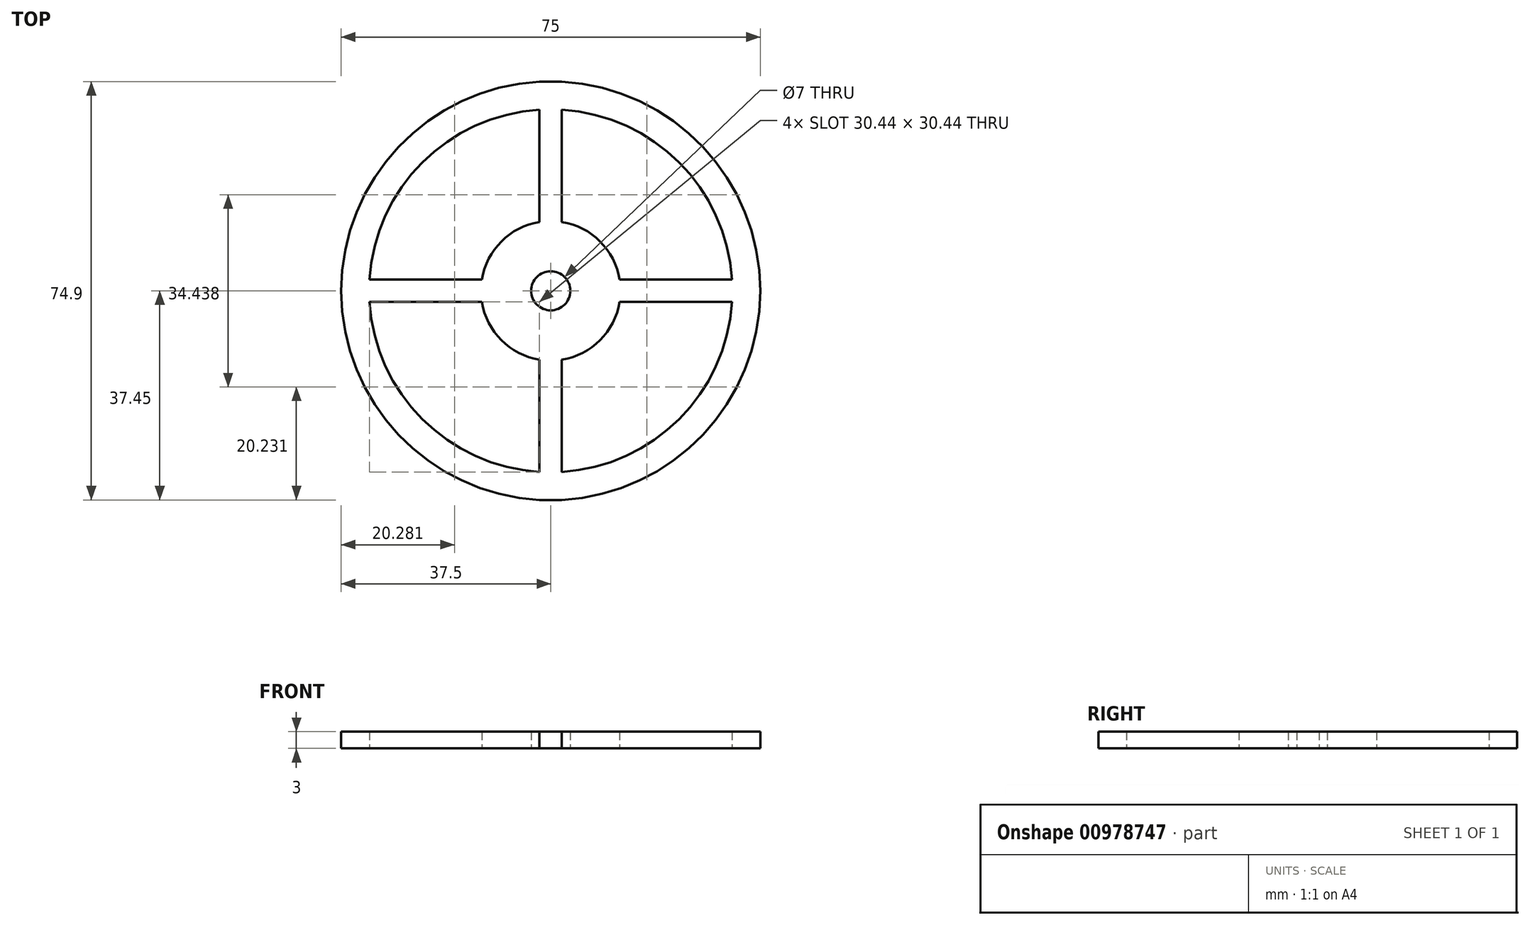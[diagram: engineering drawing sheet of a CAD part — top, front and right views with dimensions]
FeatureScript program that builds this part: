
annotation { "Feature Type Name" : "Feature", "Feature Type Description" : "" }
export const myFeature = defineFeature(function(context is Context, id is Id, definition is map)
    precondition{}
    {
        {
            var Q0;
            Q0=qCreatedBy(makeId("Top.planeOp"),FACE);
            var sketch = newSketch(context, id + "F0", { "sketchPlane" : qUnion([Q0])});
            skCircle(sketch, "E0", {"center": v(0, 0) * mm, "radius": 37.5 * mm});
            skCircle(sketch, "E1", {"center": v(0, 0) * mm, "radius": 3.5 * mm});
            skLineSegment(sketch, "E2", {"start": v(0, 0) * mm, "end": v(0, 37.5) * mm, "construction": true});
            skLineSegment(sketch, "E3", {"start": v(0, 0) * mm, "end": v(0, -37.5) * mm, "construction": true});
            skLineSegment(sketch, "E4", {"start": v(0, 0) * mm, "end": v(-37.5, 0) * mm, "construction": true});
            skLineSegment(sketch, "E5", {"start": v(0, 0) * mm, "end": v(37.5, 0) * mm, "construction": true});
            skLineSegment(sketch, "E6.bottom", {"start": v(-2, 2) * mm, "end": v(2, 2) * mm, "construction": true});
            skLineSegment(sketch, "E6.top", {"start": v(-2, -2) * mm, "end": v(2, -2) * mm, "construction": true});
            skLineSegment(sketch, "E6.left", {"start": v(-2, 2) * mm, "end": v(-2, -2) * mm, "construction": true});
            skLineSegment(sketch, "E6.right", {"start": v(2, 2) * mm, "end": v(2, -2) * mm, "construction": true});
            skLineSegment(sketch, "E7", {"start": v(-2, 2) * mm, "end": v(2, -2) * mm, "construction": true});
            skLineSegment(sketch, "E8.left", {"start": v(-2, 2) * mm, "end": v(-2, 0.65) * mm, "construction": true});
            skLineSegment(sketch, "E8.right", {"start": v(-37.45, -0.65) * mm, "end": v(-37.45, -2) * mm, "construction": true});
            skLineSegment(sketch, "E9.bottom", {"start": v(2, -2) * mm, "end": v(37.5, -2) * mm});
            skLineSegment(sketch, "E9.top", {"start": v(2, 2) * mm, "end": v(37.5, 2) * mm});
            skLineSegment(sketch, "E9.left", {"start": v(2, -2) * mm, "end": v(2, 2) * mm, "construction": true});
            skLineSegment(sketch, "E9.right", {"start": v(37.5, -2) * mm, "end": v(37.5, 2) * mm, "construction": true});
            skLineSegment(sketch, "E10.bottom", {"start": v(-2, 2) * mm, "end": v(-37.45, 2) * mm});
            skLineSegment(sketch, "E10.top", {"start": v(-2, -2) * mm, "end": v(-37.45, -2) * mm});
            skLineSegment(sketch, "E10.right", {"start": v(-37.45, 2) * mm, "end": v(-37.45, -2) * mm, "construction": true});
            skLineSegment(sketch, "E11.bottom", {"start": v(-2, 2) * mm, "end": v(2, 2) * mm});
            skLineSegment(sketch, "E11.top", {"start": v(-2, 37.45) * mm, "end": v(2, 37.45) * mm});
            skLineSegment(sketch, "E11.left", {"start": v(-2, 2) * mm, "end": v(-2, 37.45) * mm});
            skLineSegment(sketch, "E11.right", {"start": v(2, 2) * mm, "end": v(2, 37.45) * mm});
            skLineSegment(sketch, "E12.bottom", {"start": v(-2, -2) * mm, "end": v(2, -2) * mm});
            skLineSegment(sketch, "E12.top", {"start": v(-2, -37.45) * mm, "end": v(2, -37.45) * mm});
            skLineSegment(sketch, "E12.left", {"start": v(-2, -2) * mm, "end": v(-2, -37.45) * mm});
            skLineSegment(sketch, "E12.right", {"start": v(2, -2) * mm, "end": v(2, -37.45) * mm});
            skCircle(sketch, "E13", {"center": v(0, 0) * mm, "radius": 12.5 * mm});
            skCircle(sketch, "E14", {"center": v(0, 0) * mm, "radius": 32.5 * mm});
            skSolve(sketch);
        }
        {
            var Q0;
            {var subQ1=sQuery(id+"F0.wireOp",EDGE,"E0");var subQ3=sQuery(id+"F0.wireOp",EDGE,"E9.top");var subQ4=makeQuery(id+"F0.imprint","INTERSECT",VERTEX,{"derivedFrom":[subQ1,subQ3]});Q0=makeQuery(id+"F0.imprint","IMPRINT",FACE,{"disambiguationData":[TD([[makeQuery(id+"F0.imprint","IMPRINT",EDGE,{"disambiguationData":[TD([[subQ4,1.0]])],"derivedFrom":subQ3}),1.0]])]});}
            var Q1;
            {var subQ1=sQuery(id+"F0.wireOp",EDGE,"E0");var subQ3=sQuery(id+"F0.wireOp",EDGE,"E9.bottom");var subQ4=makeQuery(id+"F0.imprint","INTERSECT",VERTEX,{"derivedFrom":[subQ1,subQ3]});Q1=makeQuery(id+"F0.imprint","IMPRINT",FACE,{"disambiguationData":[TD([[makeQuery(id+"F0.imprint","IMPRINT",EDGE,{"disambiguationData":[TD([[subQ4,1.0]])],"derivedFrom":subQ3}),-1.0]])]});}
            var Q2;
            {var subQ0=sQuery(id+"F0.wireOp",EDGE,"E9.top");var subQ1=sQuery(id+"F0.wireOp",EDGE,"E0");var subQ2=makeQuery(id+"F0.imprint","INTERSECT",VERTEX,{"derivedFrom":[subQ1,subQ0]});Q2=makeQuery(id+"F0.imprint","IMPRINT",FACE,{"disambiguationData":[TD([[makeQuery(id+"F0.imprint","IMPRINT",EDGE,{"disambiguationData":[TD([[subQ2,1.0]])],"derivedFrom":subQ1}),1.0]])]});}
            var Q3;
            {var subQ0=sQuery(id+"F0.wireOp",EDGE,"E13");var subQ1=sQuery(id+"F0.wireOp",EDGE,"E9.bottom");var subQ2=makeQuery(id+"F0.imprint","INTERSECT",VERTEX,{"derivedFrom":[subQ1,subQ0]});Q3=makeQuery(id+"F0.imprint","IMPRINT",FACE,{"disambiguationData":[TD([[makeQuery(id+"F0.imprint","IMPRINT",EDGE,{"disambiguationData":[TD([[subQ2,-1.0]])],"derivedFrom":subQ1}),1.0]])]});}
            var Q4;
            {var subQ0=sQuery(id+"F0.wireOp",EDGE,"E9.top");var subQ1=sQuery(id+"F0.wireOp",EDGE,"E1");var subQ2=makeQuery(id+"F0.imprint","INTERSECT",VERTEX,{"derivedFrom":[subQ1,subQ0]});Q4=makeQuery(id+"F0.imprint","IMPRINT",FACE,{"disambiguationData":[TD([[makeQuery(id+"F0.imprint","IMPRINT",EDGE,{"disambiguationData":[TD([[subQ2,1.0]])],"derivedFrom":subQ1}),-1.0]])]});}
            var Q5;
            {var subQ0=sQuery(id+"F0.wireOp",EDGE,"E12.right");var subQ1=sQuery(id+"F0.wireOp",EDGE,"E1");var subQ2=makeQuery(id+"F0.imprint","INTERSECT",VERTEX,{"derivedFrom":[subQ1,subQ0]});Q5=makeQuery(id+"F0.imprint","IMPRINT",FACE,{"disambiguationData":[TD([[makeQuery(id+"F0.imprint","IMPRINT",EDGE,{"disambiguationData":[TD([[subQ2,-1.0]])],"derivedFrom":subQ1}),-1.0]])]});}
            var Q6;
            {var subQ0=sQuery(id+"F0.wireOp",EDGE,"E11.right");var subQ1=sQuery(id+"F0.wireOp",EDGE,"E1");var subQ2=makeQuery(id+"F0.imprint","INTERSECT",VERTEX,{"derivedFrom":[subQ1,subQ0]});Q6=makeQuery(id+"F0.imprint","IMPRINT",FACE,{"disambiguationData":[TD([[makeQuery(id+"F0.imprint","IMPRINT",EDGE,{"disambiguationData":[TD([[subQ2,1.0]])],"derivedFrom":subQ1}),-1.0]])]});}
            var Q7;
            {var subQ0=sQuery(id+"F0.wireOp",EDGE,"E11.left");var subQ1=sQuery(id+"F0.wireOp",EDGE,"E1");var subQ2=makeQuery(id+"F0.imprint","INTERSECT",VERTEX,{"derivedFrom":[subQ1,subQ0]});Q7=makeQuery(id+"F0.imprint","IMPRINT",FACE,{"disambiguationData":[TD([[makeQuery(id+"F0.imprint","IMPRINT",EDGE,{"disambiguationData":[TD([[subQ2,-1.0]])],"derivedFrom":subQ1}),-1.0]])]});}
            var Q8;
            {var subQ0=sQuery(id+"F0.wireOp",EDGE,"E10.bottom");var subQ1=sQuery(id+"F0.wireOp",EDGE,"E1");var subQ2=makeQuery(id+"F0.imprint","INTERSECT",VERTEX,{"derivedFrom":[subQ1,subQ0]});Q8=makeQuery(id+"F0.imprint","IMPRINT",FACE,{"disambiguationData":[TD([[makeQuery(id+"F0.imprint","IMPRINT",EDGE,{"disambiguationData":[TD([[subQ2,-1.0]])],"derivedFrom":subQ1}),-1.0]])]});}
            var Q9;
            {var subQ0=sQuery(id+"F0.wireOp",EDGE,"E10.top");var subQ1=sQuery(id+"F0.wireOp",EDGE,"E1");var subQ2=makeQuery(id+"F0.imprint","INTERSECT",VERTEX,{"derivedFrom":[subQ1,subQ0]});Q9=makeQuery(id+"F0.imprint","IMPRINT",FACE,{"disambiguationData":[TD([[makeQuery(id+"F0.imprint","IMPRINT",EDGE,{"disambiguationData":[TD([[subQ2,-1.0]])],"derivedFrom":subQ1}),-1.0]])]});}
            var Q10;
            {var subQ0=sQuery(id+"F0.wireOp",EDGE,"E11.right");var subQ1=sQuery(id+"F0.wireOp",EDGE,"E1");var subQ2=makeQuery(id+"F0.imprint","INTERSECT",VERTEX,{"derivedFrom":[subQ1,subQ0]});Q10=makeQuery(id+"F0.imprint","IMPRINT",FACE,{"disambiguationData":[TD([[makeQuery(id+"F0.imprint","IMPRINT",EDGE,{"disambiguationData":[TD([[subQ2,-1.0]])],"derivedFrom":subQ1}),-1.0]])]});}
            var Q11;
            {var subQ0=sQuery(id+"F0.wireOp",EDGE,"E12.left");var subQ1=sQuery(id+"F0.wireOp",EDGE,"E1");var subQ2=makeQuery(id+"F0.imprint","INTERSECT",VERTEX,{"derivedFrom":[subQ1,subQ0]});Q11=makeQuery(id+"F0.imprint","IMPRINT",FACE,{"disambiguationData":[TD([[makeQuery(id+"F0.imprint","IMPRINT",EDGE,{"disambiguationData":[TD([[subQ2,-1.0]])],"derivedFrom":subQ1}),-1.0]])]});}
            var Q12;
            {var subQ0=sQuery(id+"F0.wireOp",EDGE,"E13");var subQ1=sQuery(id+"F0.wireOp",EDGE,"E12.left");var subQ2=makeQuery(id+"F0.imprint","INTERSECT",VERTEX,{"derivedFrom":[subQ1,subQ0]});Q12=makeQuery(id+"F0.imprint","IMPRINT",FACE,{"disambiguationData":[TD([[makeQuery(id+"F0.imprint","IMPRINT",EDGE,{"disambiguationData":[TD([[subQ2,-1.0]])],"derivedFrom":subQ1}),1.0]])]});}
            var Q13;
            {var subQ0=sQuery(id+"F0.wireOp",EDGE,"E12.top");Q13=makeQuery(id+"F0.imprint","IMPRINT",FACE,{"disambiguationData":[TD([[makeQuery(id+"F0.imprint","IMPRINT",EDGE,{"derivedFrom":subQ0}),1.0]])]});}
            var Q14;
            {var subQ0=sQuery(id+"F0.wireOp",EDGE,"E10.top");var subQ1=sQuery(id+"F0.wireOp",EDGE,"E0");var subQ2=makeQuery(id+"F0.imprint","INTERSECT",VERTEX,{"derivedFrom":[subQ1,subQ0]});Q14=makeQuery(id+"F0.imprint","IMPRINT",FACE,{"disambiguationData":[TD([[makeQuery(id+"F0.imprint","IMPRINT",EDGE,{"disambiguationData":[TD([[subQ2,1.0]])],"derivedFrom":subQ0}),1.0]])]});}
            var Q15;
            {var subQ0=sQuery(id+"F0.wireOp",EDGE,"E10.bottom");var subQ1=sQuery(id+"F0.wireOp",EDGE,"E0");var subQ2=makeQuery(id+"F0.imprint","INTERSECT",VERTEX,{"derivedFrom":[subQ1,subQ0]});Q15=makeQuery(id+"F0.imprint","IMPRINT",FACE,{"disambiguationData":[TD([[makeQuery(id+"F0.imprint","IMPRINT",EDGE,{"disambiguationData":[TD([[subQ2,1.0]])],"derivedFrom":subQ0}),-1.0]])]});}
            var Q16;
            {var subQ0=sQuery(id+"F0.wireOp",EDGE,"E10.bottom");var subQ1=sQuery(id+"F0.wireOp",EDGE,"E0");var subQ2=makeQuery(id+"F0.imprint","INTERSECT",VERTEX,{"derivedFrom":[subQ1,subQ0]});Q16=makeQuery(id+"F0.imprint","IMPRINT",FACE,{"disambiguationData":[TD([[makeQuery(id+"F0.imprint","IMPRINT",EDGE,{"disambiguationData":[TD([[subQ2,-1.0]])],"derivedFrom":subQ1}),1.0]])]});}
            var Q17;
            {var subQ0=sQuery(id+"F0.wireOp",EDGE,"E13");var subQ1=sQuery(id+"F0.wireOp",EDGE,"E10.bottom");var subQ2=makeQuery(id+"F0.imprint","INTERSECT",VERTEX,{"derivedFrom":[subQ1,subQ0]});Q17=makeQuery(id+"F0.imprint","IMPRINT",FACE,{"disambiguationData":[TD([[makeQuery(id+"F0.imprint","IMPRINT",EDGE,{"disambiguationData":[TD([[subQ2,-1.0]])],"derivedFrom":subQ1}),1.0]])]});}
            var Q18;
            {var subQ0=sQuery(id+"F0.wireOp",EDGE,"E11.top");Q18=makeQuery(id+"F0.imprint","IMPRINT",FACE,{"disambiguationData":[TD([[makeQuery(id+"F0.imprint","IMPRINT",EDGE,{"derivedFrom":subQ0}),-1.0]])]});}
            var Q19;
            {var subQ0=sQuery(id+"F0.wireOp",EDGE,"E13");var subQ1=sQuery(id+"F0.wireOp",EDGE,"E11.left");var subQ2=makeQuery(id+"F0.imprint","INTERSECT",VERTEX,{"derivedFrom":[subQ1,subQ0]});Q19=makeQuery(id+"F0.imprint","IMPRINT",FACE,{"disambiguationData":[TD([[makeQuery(id+"F0.imprint","IMPRINT",EDGE,{"disambiguationData":[TD([[subQ2,-1.0]])],"derivedFrom":subQ1}),-1.0]])]});}
            extrude(context, id + "F1", {"entities" : qUnion([Q0, Q1, Q2, Q3, Q4, Q5, Q6, Q7, Q8, Q9, Q10, Q11, Q12, Q13, Q14, Q15, Q16, Q17, Q18, Q19]), "depth" : 3 * mm, "offsetDistance" : 25 * mm});
        }
    });
